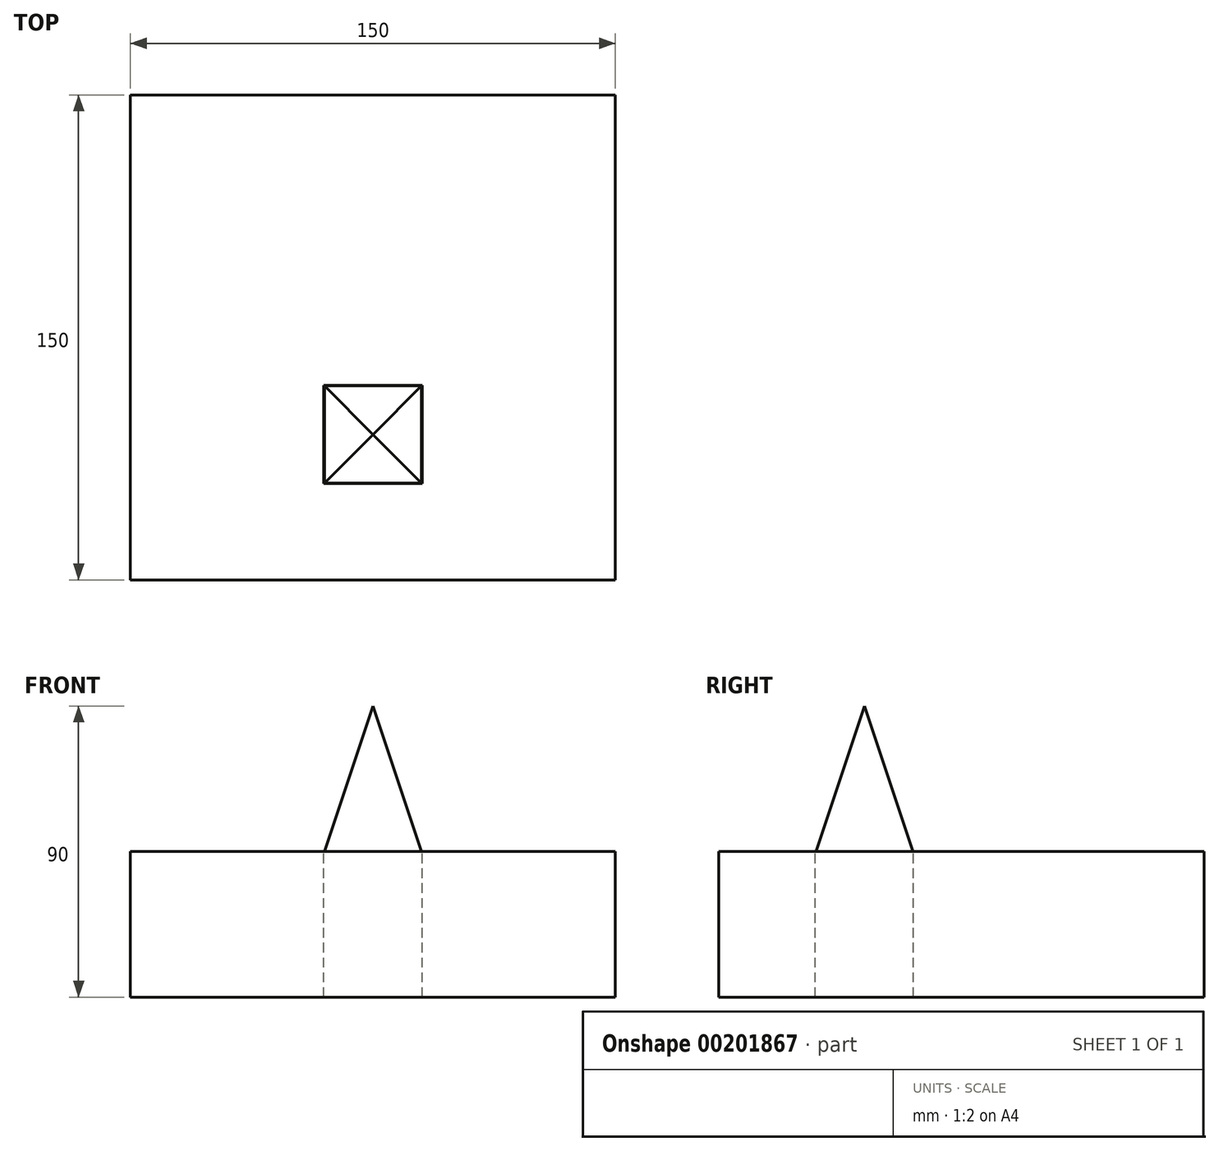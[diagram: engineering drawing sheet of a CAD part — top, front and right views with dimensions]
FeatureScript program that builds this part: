
annotation { "Feature Type Name" : "Feature", "Feature Type Description" : "" }
export const myFeature = defineFeature(function(context is Context, id is Id, definition is map)
    precondition{}
    {
        {
            var Q0;
            Q0=qCreatedBy(makeId("Top.planeOp"),FACE);
            var sketch = newSketch(context, id + "F0", { "sketchPlane" : qUnion([Q0])});
            skLineSegment(sketch, "E0.bottom", {"start": v(-91.66, 56.15) * mm, "end": v(58.34, 56.15) * mm});
            skLineSegment(sketch, "E0.top", {"start": v(-91.66, -93.85) * mm, "end": v(58.34, -93.85) * mm});
            skLineSegment(sketch, "E0.left", {"start": v(-91.66, 56.15) * mm, "end": v(-91.66, -93.85) * mm});
            skLineSegment(sketch, "E0.right", {"start": v(58.34, 56.15) * mm, "end": v(58.34, -93.85) * mm});
            skLineSegment(sketch, "E1.bottom", {"start": v(-31.86, -33.65) * mm, "end": v(-1.46, -33.65) * mm});
            skLineSegment(sketch, "E1.top", {"start": v(-31.86, -64.05) * mm, "end": v(-1.46, -64.05) * mm});
            skLineSegment(sketch, "E1.left", {"start": v(-31.86, -33.65) * mm, "end": v(-31.86, -64.05) * mm});
            skLineSegment(sketch, "E1.right", {"start": v(-1.46, -33.65) * mm, "end": v(-1.46, -64.05) * mm});
            skSolve(sketch);
        }
        {
            var Q0;
            Q0=makeQuery(id+"F0.imprint","IMPRINT",FACE,{"disambiguationData":[TD([[makeQuery(id+"F0.imprint","IMPRINT",EDGE,{"derivedFrom":sQuery(id+"F0.wireOp",EDGE,"E0.bottom")}),-1.0]])]});
            extrude(context, id + "F1", {"entities" : qUnion([Q0]), "oppositeDirection" : true, "depth" : 45 * mm});
        }
        {
            var Q0;
            Q0=qCreatedBy(makeId("Top.planeOp"),FACE);
            var sketch = newSketch(context, id + "F2", { "sketchPlane" : qUnion([Q0])});
            skLineSegment(sketch, "E2.bottom", {"start": v(-31.68, -33.85) * mm, "end": v(-1.68, -33.85) * mm});
            skLineSegment(sketch, "E2.top", {"start": v(-31.68, -63.85) * mm, "end": v(-1.68, -63.85) * mm});
            skLineSegment(sketch, "E2.left", {"start": v(-31.68, -33.85) * mm, "end": v(-31.68, -63.85) * mm});
            skLineSegment(sketch, "E2.right", {"start": v(-1.68, -33.85) * mm, "end": v(-1.68, -63.85) * mm});
            skSolve(sketch);
        }
        {
            var Q0;
            Q0=makeQuery(id+"F2.imprint","IMPRINT",FACE,{"disambiguationData":[TD([[makeQuery(id+"F2.imprint","IMPRINT",EDGE,{"derivedFrom":sQuery(id+"F2.wireOp",EDGE,"E2.bottom")}),-1.0]])]});
            extrude(context, id + "F3", {"entities" : qUnion([Q0]), "depth" : 45 * mm});
        }
        {
            var Q0;
            Q0=makeQuery(id+"F3.opExtrude","CAP_FACE",FACE,{"disambiguationData":[OSD([sQuery(id+"F2.wireOp",EDGE,"E2.bottom"),sQuery(id+"F2.wireOp",EDGE,"E2.top"),sQuery(id+"F2.wireOp",EDGE,"E2.left"),sQuery(id+"F2.wireOp",EDGE,"E2.right")])],"isStart":false});
            chamfer(context, id + "F4", {"entities" : qUnion([Q0]), "chamferType" : ChamferType.TWO_OFFSETS, "width1" : 45 * mm, "oppositeDirection" : false, "width2" : 15 * mm, "tangentPropagation" : true});
        }
    });
